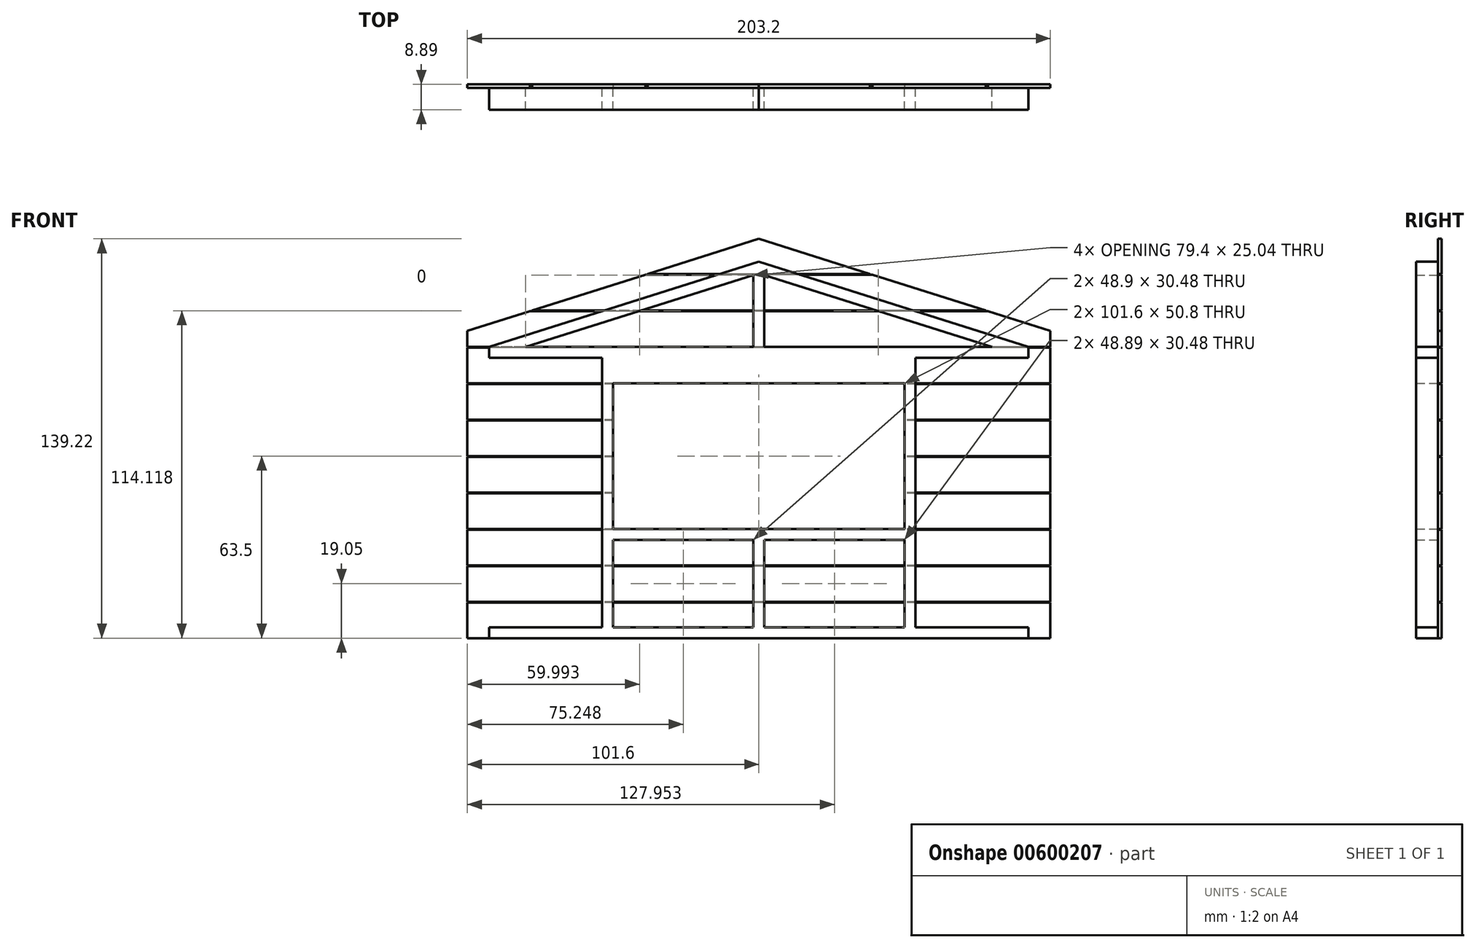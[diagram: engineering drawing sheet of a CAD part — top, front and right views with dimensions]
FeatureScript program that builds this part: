
annotation { "Feature Type Name" : "Feature", "Feature Type Description" : "" }
export const myFeature = defineFeature(function(context is Context, id is Id, definition is map)
    precondition{}
    {
        {
            var Q0;
            Q0=qCreatedBy(makeId("Front.planeOp"),FACE);
            var sketch = newSketch(context, id + "F0", { "sketchPlane" : qUnion([Q0])});
            skLineSegment(sketch, "E0.bottom", {"start": v(0, 0) * mm, "end": v(187.96, 0) * mm});
            skLineSegment(sketch, "E0.top", {"start": v(0, 3.81) * mm, "end": v(187.96, 3.81) * mm});
            skLineSegment(sketch, "E0.left", {"start": v(0, 0) * mm, "end": v(0, 3.81) * mm});
            skLineSegment(sketch, "E0.right", {"start": v(187.96, 0) * mm, "end": v(187.96, 3.81) * mm});
            skLineSegment(sketch, "E1.bottom", {"start": v(0, 101.6) * mm, "end": v(187.96, 101.6) * mm});
            skLineSegment(sketch, "E1.top", {"start": v(0, 97.8) * mm, "end": v(187.96, 97.8) * mm});
            skLineSegment(sketch, "E1.left", {"start": v(0, 101.6) * mm, "end": v(0, 97.8) * mm});
            skLineSegment(sketch, "E1.right", {"start": v(187.96, 101.6) * mm, "end": v(187.96, 97.8) * mm});
            skLineSegment(sketch, "E2.bottom", {"start": v(0, 97.8) * mm, "end": v(3.81, 97.8) * mm});
            skLineSegment(sketch, "E2.top", {"start": v(0, 3.81) * mm, "end": v(3.81, 3.81) * mm});
            skLineSegment(sketch, "E2.left", {"start": v(0, 97.8) * mm, "end": v(0, 3.81) * mm});
            skLineSegment(sketch, "E2.right", {"start": v(3.81, 97.8) * mm, "end": v(3.81, 3.81) * mm});
            skLineSegment(sketch, "E3.bottom", {"start": v(187.96, 97.8) * mm, "end": v(184.15, 97.8) * mm});
            skLineSegment(sketch, "E3.top", {"start": v(187.96, 3.81) * mm, "end": v(184.15, 3.81) * mm});
            skLineSegment(sketch, "E3.left", {"start": v(187.96, 97.8) * mm, "end": v(187.96, 3.81) * mm});
            skLineSegment(sketch, "E3.right", {"start": v(184.15, 97.8) * mm, "end": v(184.15, 3.81) * mm});
            skLineSegment(sketch, "E4", {"start": v(39.37, 97.8) * mm, "end": v(39.37, 3.81) * mm});
            skLineSegment(sketch, "E5", {"start": v(43.18, 97.8) * mm, "end": v(43.18, 3.81) * mm});
            skLineSegment(sketch, "E6", {"start": v(148.6, 97.8) * mm, "end": v(148.6, 3.81) * mm});
            skLineSegment(sketch, "E7", {"start": v(144.78, 97.8) * mm, "end": v(144.78, 3.81) * mm});
            skLineSegment(sketch, "E8", {"start": v(43.18, 92.7) * mm, "end": v(144.78, 92.71) * mm});
            skLineSegment(sketch, "E9", {"start": v(43.18, 88.9) * mm, "end": v(144.78, 88.9) * mm});
            skLineSegment(sketch, "E10", {"start": v(43.18, 38.1) * mm, "end": v(144.78, 38.1) * mm});
            skLineSegment(sketch, "E11", {"start": v(43.18, 34.3) * mm, "end": v(144.78, 34.3) * mm});
            skLineSegment(sketch, "E12", {"start": v(95.89, 34.3) * mm, "end": v(95.89, 3.81) * mm});
            skLineSegment(sketch, "E13", {"start": v(92.08, 34.3) * mm, "end": v(92.08, 3.81) * mm});
            skLineSegment(sketch, "E14", {"start": v(0, 101.6) * mm, "end": v(93.98, 131.23) * mm});
            skLineSegment(sketch, "E15", {"start": v(93.98, 131.23) * mm, "end": v(187.96, 101.6) * mm});
            skLineSegment(sketch, "E16", {"start": v(12.67, 101.6) * mm, "end": v(93.98, 127.24) * mm});
            skLineSegment(sketch, "E17", {"start": v(93.98, 127.24) * mm, "end": v(175.29, 101.6) * mm});
            skLineSegment(sketch, "E18", {"start": v(92.08, 101.6) * mm, "end": v(92.08, 126.64) * mm});
            skLineSegment(sketch, "E19", {"start": v(95.89, 101.6) * mm, "end": v(95.89, 126.64) * mm});
            skSolve(sketch);
        }
        {
            var Q0;
            Q0=makeQuery(id+"F0.imprint","IMPRINT",FACE,{"disambiguationData":[TD([[makeQuery(id+"F0.imprint","IMPRINT",EDGE,{"derivedFrom":sQuery(id+"F0.wireOp",EDGE,"E1.bottom")}),-1.0]])]});
            var Q1;
            Q1=makeQuery(id+"F0.imprint","IMPRINT",FACE,{"disambiguationData":[TD([[makeQuery(id+"F0.imprint","IMPRINT",EDGE,{"derivedFrom":sQuery(id+"F0.wireOp",EDGE,"E2.bottom")}),-1.0]])]});
            var Q2;
            {var subQ4=sQuery(id+"F0.wireOp",EDGE,"E4");Q2=makeQuery(id+"F0.imprint","IMPRINT",FACE,{"disambiguationData":[TD([[makeQuery(id+"F0.imprint","IMPRINT",EDGE,{"derivedFrom":subQ4}),1.0]])]});}
            var Q3;
            {var subQ5=sQuery(id+"F0.wireOp",EDGE,"E9");Q3=makeQuery(id+"F0.imprint","IMPRINT",FACE,{"disambiguationData":[TD([[makeQuery(id+"F0.imprint","IMPRINT",EDGE,{"derivedFrom":subQ5}),1.0]])]});}
            var Q4;
            {var subQ0=sQuery(id+"F0.wireOp",EDGE,"Q317AGpo-LEgm-Lz7g-jjtO-wOYiPAvgsR3q");Q4=makeQuery(id+"F0.imprint","IMPRINT",FACE,{"disambiguationData":[TD([[makeQuery(id+"F0.imprint","IMPRINT",EDGE,{"derivedFrom":subQ0}),-1.0]])]});}
            var Q5;
            {var subQ4=sQuery(id+"F0.wireOp",EDGE,"E6");Q5=makeQuery(id+"F0.imprint","IMPRINT",FACE,{"disambiguationData":[TD([[makeQuery(id+"F0.imprint","IMPRINT",EDGE,{"derivedFrom":subQ4}),-1.0]])]});}
            var Q6;
            Q6=makeQuery(id+"F0.imprint","IMPRINT",FACE,{"disambiguationData":[TD([[makeQuery(id+"F0.imprint","IMPRINT",EDGE,{"derivedFrom":sQuery(id+"F0.wireOp",EDGE,"E3.bottom")}),1.0]])]});
            var Q7;
            {var subQ4=sQuery(id+"F0.wireOp",EDGE,"E10");Q7=makeQuery(id+"F0.imprint","IMPRINT",FACE,{"disambiguationData":[TD([[makeQuery(id+"F0.imprint","IMPRINT",EDGE,{"derivedFrom":subQ4}),-1.0]])]});}
            var Q8;
            {var subQ0=sQuery(id+"F0.wireOp",EDGE,"E12");Q8=makeQuery(id+"F0.imprint","IMPRINT",FACE,{"disambiguationData":[TD([[makeQuery(id+"F0.imprint","IMPRINT",EDGE,{"derivedFrom":subQ0}),-1.0]])]});}
            var Q9;
            Q9=makeQuery(id+"F0.imprint","IMPRINT",FACE,{"disambiguationData":[TD([[makeQuery(id+"F0.imprint","IMPRINT",EDGE,{"derivedFrom":sQuery(id+"F0.wireOp",EDGE,"E0.bottom")}),1.0]])]});
            var Q10;
            {var subQ4=sQuery(id+"F0.wireOp",EDGE,"E14");Q10=makeQuery(id+"F0.imprint","IMPRINT",FACE,{"disambiguationData":[TD([[makeQuery(id+"F0.imprint","IMPRINT",EDGE,{"derivedFrom":subQ4}),-1.0]])]});}
            var Q11;
            {var subQ0=sQuery(id+"F0.wireOp",EDGE,"E18");Q11=makeQuery(id+"F0.imprint","IMPRINT",FACE,{"disambiguationData":[TD([[makeQuery(id+"F0.imprint","IMPRINT",EDGE,{"derivedFrom":subQ0}),-1.0]])]});}
            var Q12;
            {var subQ5=sQuery(id+"F0.wireOp",EDGE,"E8");Q12=makeQuery(id+"F0.imprint","IMPRINT",FACE,{"disambiguationData":[TD([[makeQuery(id+"F0.imprint","IMPRINT",EDGE,{"derivedFrom":subQ5}),1.0]])]});}
            extrude(context, id + "F1", {"entities" : qUnion([Q0, Q1, Q2, Q3, Q4, Q5, Q6, Q7, Q8, Q9, Q10, Q11, Q12]), "depth" : 7.62 * mm, "offsetDistance" : 25.4 * mm});
        }
        {
            var Q0;
            Q0=qCreatedBy(makeId("Front.planeOp"),FACE);
            var sketch = newSketch(context, id + "F2", { "sketchPlane" : qUnion([Q0])});
            skLineSegment(sketch, "E20.bottom", {"start": v(195.58, 0) * mm, "end": v(-7.62, 0) * mm});
            skLineSegment(sketch, "E20.top", {"start": v(195.58, 12.45) * mm, "end": v(-7.62, 12.45) * mm});
            skLineSegment(sketch, "E20.left", {"start": v(195.58, 0) * mm, "end": v(195.58, 12.45) * mm});
            skLineSegment(sketch, "E20.right", {"start": v(-7.62, 0) * mm, "end": v(-7.62, 12.45) * mm});
            skLineSegment(sketch, "E21.0.1.0", {"start": v(195.58, 12.7) * mm, "end": v(195.58, 25.15) * mm});
            skLineSegment(sketch, "E21.0.1.1", {"start": v(195.58, 25.15) * mm, "end": v(-7.62, 25.15) * mm});
            skLineSegment(sketch, "E21.0.1.2", {"start": v(195.58, 12.7) * mm, "end": v(-7.62, 12.7) * mm});
            skLineSegment(sketch, "E21.0.1.3", {"start": v(-7.62, 12.7) * mm, "end": v(-7.62, 25.15) * mm});
            skLineSegment(sketch, "E21.0.2.0", {"start": v(195.58, 25.4) * mm, "end": v(195.58, 37.85) * mm});
            skLineSegment(sketch, "E21.0.2.1", {"start": v(195.58, 37.85) * mm, "end": v(-7.62, 37.85) * mm});
            skLineSegment(sketch, "E21.0.2.2", {"start": v(195.58, 25.4) * mm, "end": v(-7.62, 25.4) * mm});
            skLineSegment(sketch, "E21.0.2.3", {"start": v(-7.62, 25.4) * mm, "end": v(-7.62, 37.85) * mm});
            skLineSegment(sketch, "E21.0.3.0", {"start": v(195.58, 38.1) * mm, "end": v(195.58, 50.55) * mm});
            skLineSegment(sketch, "E21.0.3.1", {"start": v(195.58, 50.55) * mm, "end": v(-7.62, 50.55) * mm});
            skLineSegment(sketch, "E21.0.3.2", {"start": v(195.58, 38.1) * mm, "end": v(-7.62, 38.1) * mm});
            skLineSegment(sketch, "E21.0.3.3", {"start": v(-7.62, 38.1) * mm, "end": v(-7.62, 50.55) * mm});
            skLineSegment(sketch, "E21.0.4.0", {"start": v(195.58, 50.8) * mm, "end": v(195.58, 63.25) * mm});
            skLineSegment(sketch, "E21.0.4.1", {"start": v(195.58, 63.25) * mm, "end": v(-7.62, 63.25) * mm});
            skLineSegment(sketch, "E21.0.4.2", {"start": v(195.58, 50.8) * mm, "end": v(-7.62, 50.8) * mm});
            skLineSegment(sketch, "E21.0.4.3", {"start": v(-7.62, 50.8) * mm, "end": v(-7.62, 63.25) * mm});
            skLineSegment(sketch, "E21.0.5.0", {"start": v(195.58, 63.5) * mm, "end": v(195.58, 75.95) * mm});
            skLineSegment(sketch, "E21.0.5.1", {"start": v(195.58, 75.95) * mm, "end": v(-7.62, 75.95) * mm});
            skLineSegment(sketch, "E21.0.5.2", {"start": v(195.58, 63.5) * mm, "end": v(-7.62, 63.5) * mm});
            skLineSegment(sketch, "E21.0.5.3", {"start": v(-7.62, 63.5) * mm, "end": v(-7.62, 75.95) * mm});
            skLineSegment(sketch, "E21.0.6.0", {"start": v(195.58, 76.2) * mm, "end": v(195.58, 88.65) * mm});
            skLineSegment(sketch, "E21.0.6.1", {"start": v(195.58, 88.65) * mm, "end": v(-7.62, 88.65) * mm});
            skLineSegment(sketch, "E21.0.6.2", {"start": v(195.58, 76.2) * mm, "end": v(-7.62, 76.2) * mm});
            skLineSegment(sketch, "E21.0.6.3", {"start": v(-7.62, 76.2) * mm, "end": v(-7.62, 88.65) * mm});
            skLineSegment(sketch, "E21.0.7.0", {"start": v(195.58, 88.9) * mm, "end": v(195.58, 101.35) * mm});
            skLineSegment(sketch, "E21.0.7.1", {"start": v(195.58, 101.35) * mm, "end": v(-7.62, 101.35) * mm});
            skLineSegment(sketch, "E21.0.7.2", {"start": v(195.58, 88.9) * mm, "end": v(-7.62, 88.9) * mm});
            skLineSegment(sketch, "E21.0.7.3", {"start": v(-7.62, 88.9) * mm, "end": v(-7.62, 101.35) * mm});
            skLineSegment(sketch, "E21.direction1", {"start": v(195.58, 0) * mm, "end": v(220.98, 0) * mm, "construction": true});
            skLineSegment(sketch, "E21.direction2", {"start": v(195.58, 0) * mm, "end": v(195.58, 12.7) * mm, "construction": true});
            skLineSegment(sketch, "E22.0.0.8", {"start": v(195.58, 101.6) * mm, "end": v(195.58, 114.05) * mm});
            skLineSegment(sketch, "E22.3.0.8", {"start": v(195.58, 114.05) * mm, "end": v(-7.62, 114.05) * mm});
            skLineSegment(sketch, "E22.6.0.8", {"start": v(195.58, 101.6) * mm, "end": v(-7.62, 101.6) * mm});
            skLineSegment(sketch, "E22.9.0.8", {"start": v(-7.62, 101.6) * mm, "end": v(-7.62, 114.05) * mm});
            skLineSegment(sketch, "E22.0.0.9", {"start": v(195.58, 114.3) * mm, "end": v(195.58, 126.75) * mm});
            skLineSegment(sketch, "E22.3.0.9", {"start": v(195.58, 126.75) * mm, "end": v(-7.62, 126.75) * mm});
            skLineSegment(sketch, "E22.6.0.9", {"start": v(195.58, 114.3) * mm, "end": v(-7.62, 114.3) * mm});
            skLineSegment(sketch, "E22.9.0.9", {"start": v(-7.62, 114.3) * mm, "end": v(-7.62, 126.75) * mm});
            skLineSegment(sketch, "E23.0.0.10", {"start": v(195.58, 127) * mm, "end": v(195.58, 139.45) * mm});
            skLineSegment(sketch, "E23.3.0.10", {"start": v(195.58, 139.45) * mm, "end": v(-7.62, 139.45) * mm});
            skLineSegment(sketch, "E23.6.0.10", {"start": v(195.58, 127) * mm, "end": v(-7.62, 127) * mm});
            skLineSegment(sketch, "E23.9.0.10", {"start": v(-7.62, 127) * mm, "end": v(-7.62, 139.45) * mm});
            skSolve(sketch);
        }
        {
            var Q0;
            Q0 = qSketchRegion(id + "F2", true);
            extrude(context, id + "F3", {"entities" : qUnion([Q0]), "oppositeDirection" : true, "depth" : 1.27 * mm, "offsetDistance" : 25.4 * mm});
        }
        {
            var Q0;
            {var subQ0=sQuery(id+"F0.wireOp",EDGE,"E9");Q0=makeQuery(id+"F0.imprint","IMPRINT",FACE,{"disambiguationData":[TD([[makeQuery(id+"F0.imprint","IMPRINT",EDGE,{"derivedFrom":subQ0}),-1.0]])]});}
            extrude(context, id + "F4", {"entities" : qUnion([Q0]), "operationType" : NewBodyOperationType.REMOVE, "oppositeDirection" : true, "depth" : 25.4 * mm, "offsetDistance" : 25.4 * mm});
        }
        {
            var Q0;
            Q0=qCreatedBy(makeId("Front.planeOp"),FACE);
            var sketch = newSketch(context, id + "F5", { "sketchPlane" : qUnion([Q0])});
            skLineSegment(sketch, "E24", {"start": v(-10.16, 106.39) * mm, "end": v(93.98, 139.22) * mm});
            skLineSegment(sketch, "E25", {"start": v(93.98, 139.22) * mm, "end": v(198.12, 106.39) * mm});
            skLineSegment(sketch, "E26", {"start": v(198.12, 106.39) * mm, "end": v(198.12, 141.6) * mm});
            skLineSegment(sketch, "E27", {"start": v(198.12, 141.6) * mm, "end": v(-10.16, 141.6) * mm});
            skLineSegment(sketch, "E28", {"start": v(-10.16, 141.6) * mm, "end": v(-10.16, 106.39) * mm});
            skSolve(sketch);
        }
        {
            var Q0;
            Q0=makeQuery(id+"F5.imprint","IMPRINT",FACE,{"disambiguationData":[TD([[makeQuery(id+"F5.imprint","IMPRINT",EDGE,{"derivedFrom":sQuery(id+"F5.wireOp",EDGE,"E24")}),1.0]])]});
            extrude(context, id + "F6", {"entities" : qUnion([Q0]), "operationType" : NewBodyOperationType.REMOVE, "oppositeDirection" : true, "depth" : 2.54 * mm, "offsetDistance" : 25.4 * mm});
        }
    });
